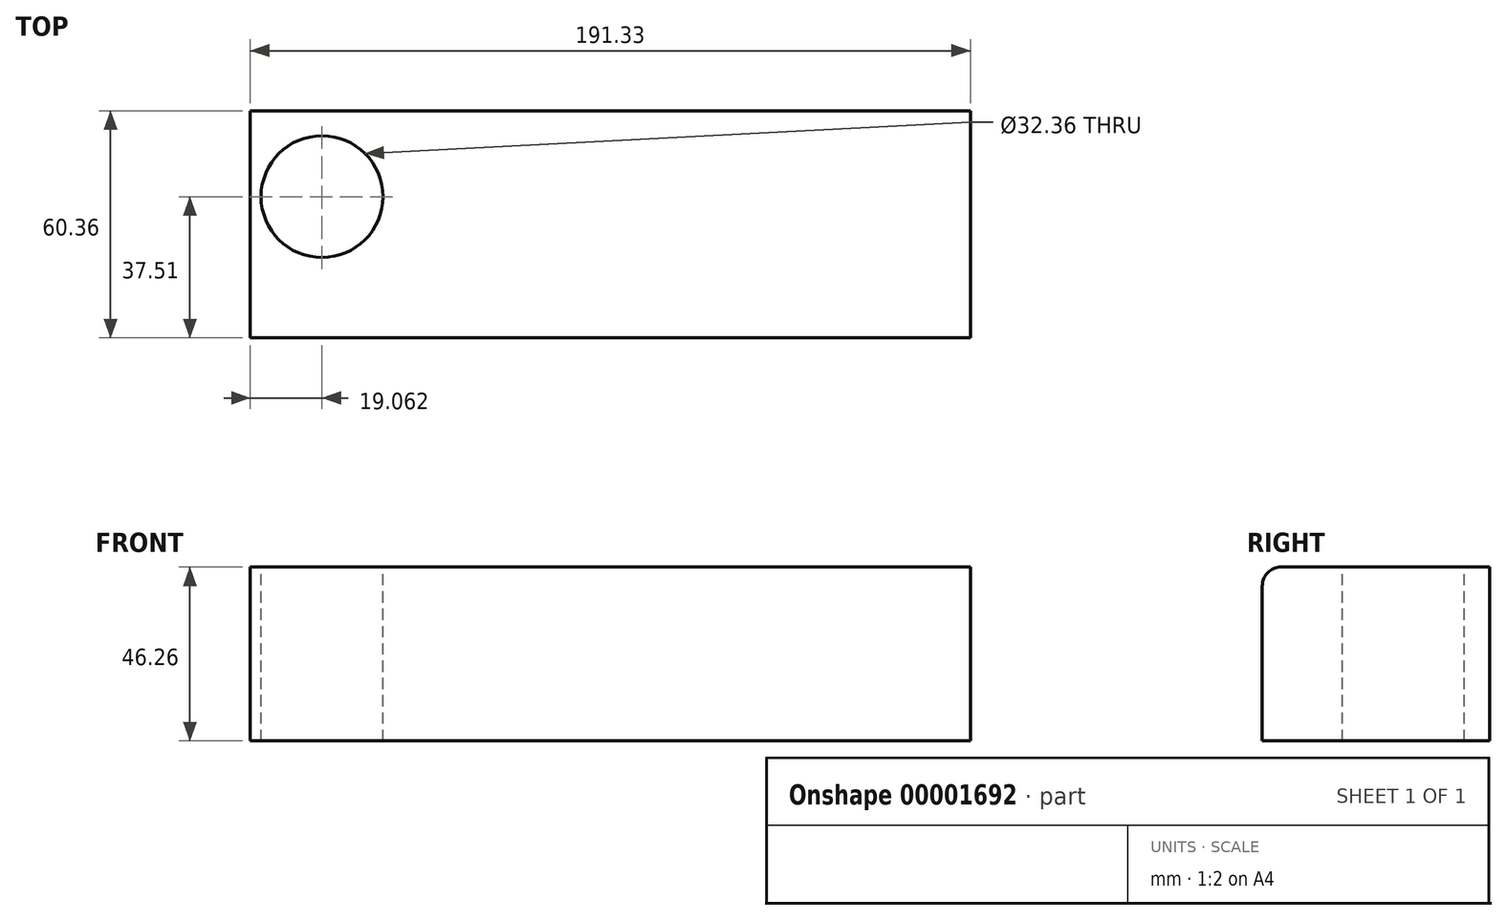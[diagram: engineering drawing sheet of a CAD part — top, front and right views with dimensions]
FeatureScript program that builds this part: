
annotation { "Feature Type Name" : "Feature", "Feature Type Description" : "" }
export const myFeature = defineFeature(function(context is Context, id is Id, definition is map)
    precondition{}
    {
        {
            var Q0;
            Q0=qCreatedBy(makeId("Top.planeOp"),FACE);
            var sketch = newSketch(context, id + "F0", { "sketchPlane" : qUnion([Q0])});
            skLineSegment(sketch, "E0.bottom", {"start": v(-76.2, 9.47) * mm, "end": v(115.12, 9.47) * mm});
            skLineSegment(sketch, "E0.top", {"start": v(-76.2, -50.9) * mm, "end": v(115.12, -50.9) * mm});
            skLineSegment(sketch, "E0.left", {"start": v(-76.2, 9.47) * mm, "end": v(-76.2, -50.9) * mm});
            skLineSegment(sketch, "E0.right", {"start": v(115.12, 9.47) * mm, "end": v(115.12, -50.9) * mm});
            skSolve(sketch);
        }
        {
            var Q0;
            Q0=makeQuery(id+"F0.imprint","IMPRINT",FACE,{"disambiguationData":[TD([[makeQuery(id+"F0.imprint","IMPRINT",EDGE,{"derivedFrom":sQuery(id+"F0.wireOp",EDGE,"E0.bottom")}),-1.0]])]});
            extrude(context, id + "F1", {"entities" : qUnion([Q0]), "depth" : 46.26 * mm});
        }
        {
            var Q0;
            Q0=makeQuery(id+"F1.opExtrude","CAP_FACE",FACE,{"disambiguationData":[OSD([sQuery(id+"F0.wireOp",EDGE,"E0.bottom"),sQuery(id+"F0.wireOp",EDGE,"E0.top"),sQuery(id+"F0.wireOp",EDGE,"E0.left"),sQuery(id+"F0.wireOp",EDGE,"E0.right")])],"isStart":false});
            var sketch = newSketch(context, id + "F2", { "sketchPlane" : qUnion([Q0])});
            skCircle(sketch, "E1", {"center": v(-57.15, -13.38) * mm, "radius": 16.18 * mm});
            skSolve(sketch);
        }
        {
            var Q0;
            Q0 = qSketchRegion(id + "F2", true);
            extrude(context, id + "F3", {"entities" : qUnion([Q0]), "operationType" : NewBodyOperationType.REMOVE, "oppositeDirection" : true, "depth" : 50.23 * mm});
        }
        {
            var Q0;
            Q0=makeQuery(id+"F1.opExtrude","CAP_EDGE",EDGE,{"disambiguationData":[OSD([sQuery(id+"F0.wireOp",EDGE,"E0.top")])],"isStart":false});
            fillet(context, id + "F4", {"entities" : qUnion([Q0]), "radius" : 5.08 * mm, "tangentPropagation" : true, "allowEdgeOverflow" : false});
        }
    });
